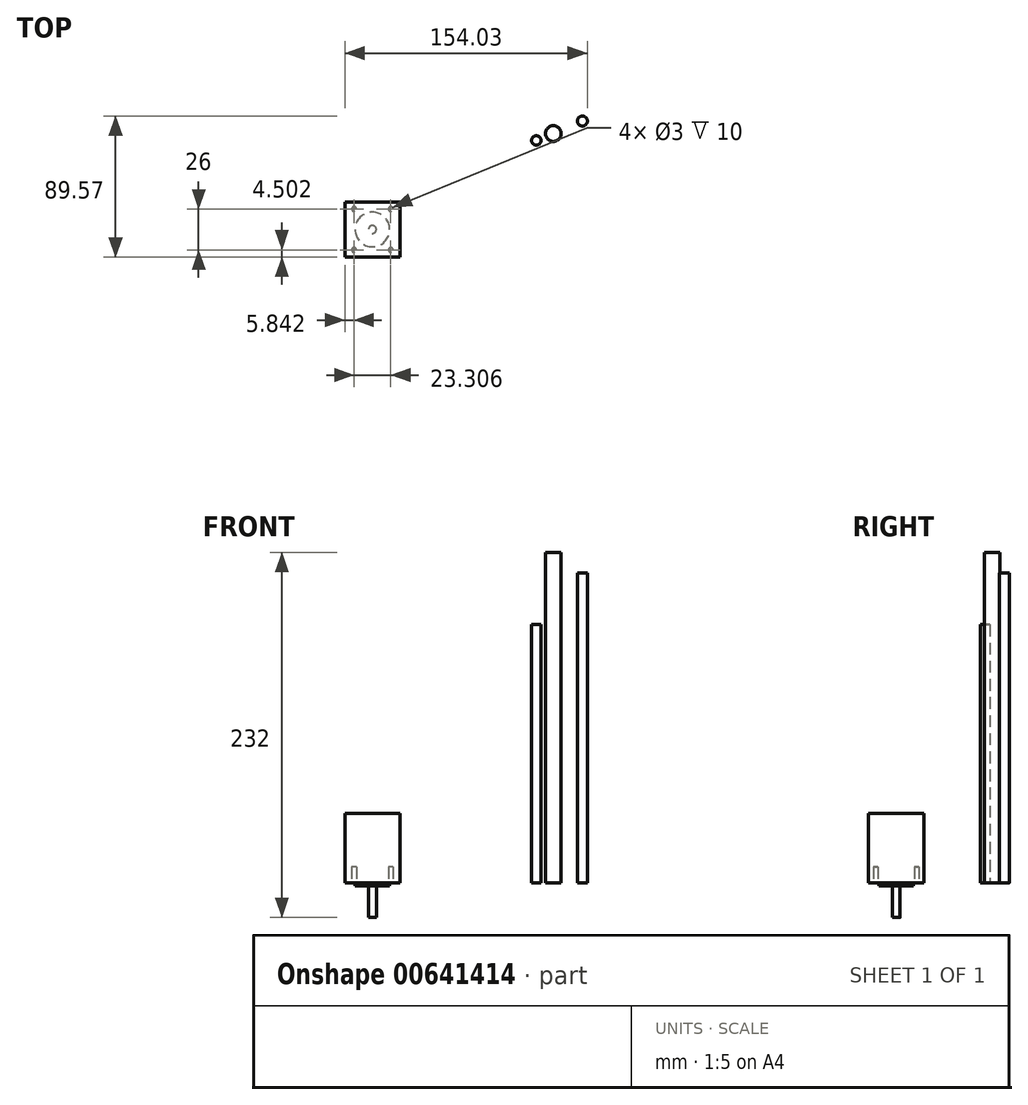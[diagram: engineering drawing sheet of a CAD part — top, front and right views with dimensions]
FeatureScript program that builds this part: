
annotation { "Feature Type Name" : "Feature", "Feature Type Description" : "" }
export const myFeature = defineFeature(function(context is Context, id is Id, definition is map)
    precondition{}
    {
        {
            var Q0;
            Q0=qCreatedBy(makeId("Top.planeOp"),FACE);
            var sketch = newSketch(context, id + "F0", { "sketchPlane" : qUnion([Q0])});
            skCircle(sketch, "E0", {"center": v(-57.47, 27.66) * mm, "radius": 3 * mm});
            skCircle(sketch, "E1", {"center": v(-46.64, 32.07) * mm, "radius": 5 * mm});
            skCircle(sketch, "E2", {"center": v(-28.18, 40.02) * mm, "radius": 3.18 * mm});
            skLineSegment(sketch, "E3.bottom", {"start": v(-144.04, -46.37) * mm, "end": v(-179.04, -46.37) * mm});
            skLineSegment(sketch, "E3.top", {"start": v(-144.04, -11.37) * mm, "end": v(-179.04, -11.37) * mm});
            skLineSegment(sketch, "E3.left", {"start": v(-144.04, -46.37) * mm, "end": v(-144.04, -11.37) * mm});
            skLineSegment(sketch, "E3.right", {"start": v(-179.04, -46.37) * mm, "end": v(-179.04, -11.37) * mm});
            skCircle(sketch, "E4", {"center": v(-161.54, -28.87) * mm, "radius": 11 * mm});
            skPoint(sketch, "E4.centerSnap0", {"position": v(-179.04, -28.87) * mm});
            skPoint(sketch, "E4.centerSnap1", {"position": v(-161.54, -11.37) * mm});
            skCircle(sketch, "E5", {"center": v(-173.2, -15.87) * mm, "radius": 1.5 * mm});
            skCircle(sketch, "E6", {"center": v(-149.9, -15.87) * mm, "radius": 1.5 * mm});
            skCircle(sketch, "E7", {"center": v(-149.9, -41.87) * mm, "radius": 1.5 * mm});
            skCircle(sketch, "E8", {"center": v(-173.2, -41.87) * mm, "radius": 1.5 * mm});
            skLineSegment(sketch, "E9", {"start": v(-161.54, -11.37) * mm, "end": v(-161.54, -17.87) * mm, "construction": true});
            skLineSegment(sketch, "E10", {"start": v(-179.04, -28.87) * mm, "end": v(-172.54, -28.87) * mm, "construction": true});
            skCircle(sketch, "E11", {"center": v(-161.54, -28.87) * mm, "radius": 2.5 * mm});
            skSolve(sketch);
        }
        {
            var Q0;
            Q0=makeQuery(id+"F0.imprint","IMPRINT",FACE,{"disambiguationData":[TD([[makeQuery(id+"F0.imprint","IMPRINT",EDGE,{"derivedFrom":sQuery(id+"F0.wireOp",EDGE,"E0")}),1.0]])]});
            extrude(context, id + "F1", {"entities" : qUnion([Q0]), "depth" : 164 * mm, "offsetDistance" : 25 * mm});
        }
        {
            var Q0;
            Q0=makeQuery(id+"F0.imprint","IMPRINT",FACE,{"disambiguationData":[TD([[makeQuery(id+"F0.imprint","IMPRINT",EDGE,{"derivedFrom":sQuery(id+"F0.wireOp",EDGE,"E1")}),1.0]])]});
            extrude(context, id + "F2", {"entities" : qUnion([Q0]), "depth" : 210 * mm, "offsetDistance" : 25 * mm});
        }
        {
            var Q0;
            Q0=makeQuery(id+"F0.imprint","IMPRINT",FACE,{"disambiguationData":[TD([[makeQuery(id+"F0.imprint","IMPRINT",EDGE,{"derivedFrom":sQuery(id+"F0.wireOp",EDGE,"E2")}),1.0]])]});
            extrude(context, id + "F3", {"entities" : qUnion([Q0]), "depth" : 196.85 * mm, "offsetDistance" : 25 * mm});
        }
        {
            var Q0;
            Q0=makeQuery(id+"F0.imprint","IMPRINT",FACE,{"disambiguationData":[TD([[makeQuery(id+"F0.imprint","IMPRINT",EDGE,{"derivedFrom":sQuery(id+"F0.wireOp",EDGE,"E3.bottom")}),-1.0]])]});
            var Q1;
            Q1=makeQuery(id+"F0.imprint","IMPRINT",FACE,{"disambiguationData":[TD([[makeQuery(id+"F0.imprint","IMPRINT",EDGE,{"derivedFrom":sQuery(id+"F0.wireOp",EDGE,"E4")}),1.0]])]});
            var Q2;
            Q2=makeQuery(id+"F0.imprint","IMPRINT",FACE,{"disambiguationData":[TD([[makeQuery(id+"F0.imprint","IMPRINT",EDGE,{"derivedFrom":sQuery(id+"F0.wireOp",EDGE,"E11")}),1.0]])]});
            var Q3;
            Q3=makeQuery(id+"F0.imprint","IMPRINT",FACE,{"disambiguationData":[TD([[makeQuery(id+"F0.imprint","IMPRINT",EDGE,{"derivedFrom":sQuery(id+"F0.wireOp",EDGE,"E7")}),1.0]])]});
            var Q4;
            Q4=makeQuery(id+"F0.imprint","IMPRINT",FACE,{"disambiguationData":[TD([[makeQuery(id+"F0.imprint","IMPRINT",EDGE,{"derivedFrom":sQuery(id+"F0.wireOp",EDGE,"E8")}),1.0]])]});
            var Q5;
            Q5=makeQuery(id+"F0.imprint","IMPRINT",FACE,{"disambiguationData":[TD([[makeQuery(id+"F0.imprint","IMPRINT",EDGE,{"derivedFrom":sQuery(id+"F0.wireOp",EDGE,"E5")}),1.0]])]});
            var Q6;
            Q6=makeQuery(id+"F0.imprint","IMPRINT",FACE,{"disambiguationData":[TD([[makeQuery(id+"F0.imprint","IMPRINT",EDGE,{"derivedFrom":sQuery(id+"F0.wireOp",EDGE,"E6")}),1.0]])]});
            extrude(context, id + "F4", {"entities" : qUnion([Q0, Q1, Q2, Q3, Q4, Q5, Q6]), "depth" : 44 * mm, "offsetDistance" : 25 * mm});
        }
        {
            var Q0;
            Q0=makeQuery(id+"F0.imprint","IMPRINT",FACE,{"disambiguationData":[TD([[makeQuery(id+"F0.imprint","IMPRINT",EDGE,{"derivedFrom":sQuery(id+"F0.wireOp",EDGE,"E4")}),1.0]])]});
            var Q1;
            Q1=makeQuery(id+"F0.imprint","IMPRINT",FACE,{"disambiguationData":[TD([[makeQuery(id+"F0.imprint","IMPRINT",EDGE,{"derivedFrom":sQuery(id+"F0.wireOp",EDGE,"E11")}),1.0]])]});
            extrude(context, id + "F5", {"entities" : qUnion([Q0, Q1]), "operationType" : NewBodyOperationType.ADD, "oppositeDirection" : true, "depth" : 2 * mm, "offsetDistance" : 25 * mm});
        }
        {
            var Q0;
            Q0=makeQuery(id+"F0.imprint","IMPRINT",FACE,{"disambiguationData":[TD([[makeQuery(id+"F0.imprint","IMPRINT",EDGE,{"derivedFrom":sQuery(id+"F0.wireOp",EDGE,"E8")}),1.0]])]});
            var Q1;
            Q1=makeQuery(id+"F0.imprint","IMPRINT",FACE,{"disambiguationData":[TD([[makeQuery(id+"F0.imprint","IMPRINT",EDGE,{"derivedFrom":sQuery(id+"F0.wireOp",EDGE,"E7")}),1.0]])]});
            var Q2;
            Q2=makeQuery(id+"F0.imprint","IMPRINT",FACE,{"disambiguationData":[TD([[makeQuery(id+"F0.imprint","IMPRINT",EDGE,{"derivedFrom":sQuery(id+"F0.wireOp",EDGE,"E6")}),1.0]])]});
            var Q3;
            Q3=makeQuery(id+"F0.imprint","IMPRINT",FACE,{"disambiguationData":[TD([[makeQuery(id+"F0.imprint","IMPRINT",EDGE,{"derivedFrom":sQuery(id+"F0.wireOp",EDGE,"E5")}),1.0]])]});
            extrude(context, id + "F6", {"entities" : qUnion([Q0, Q1, Q2, Q3]), "operationType" : NewBodyOperationType.REMOVE, "depth" : 10 * mm, "offsetDistance" : 25 * mm});
        }
        {
            var Q0;
            Q0=makeQuery(id+"F0.imprint","IMPRINT",FACE,{"disambiguationData":[TD([[makeQuery(id+"F0.imprint","IMPRINT",EDGE,{"derivedFrom":sQuery(id+"F0.wireOp",EDGE,"E11")}),1.0]])]});
            extrude(context, id + "F7", {"entities" : qUnion([Q0]), "operationType" : NewBodyOperationType.ADD, "oppositeDirection" : true, "depth" : 22 * mm, "offsetDistance" : 25 * mm});
        }
    });
